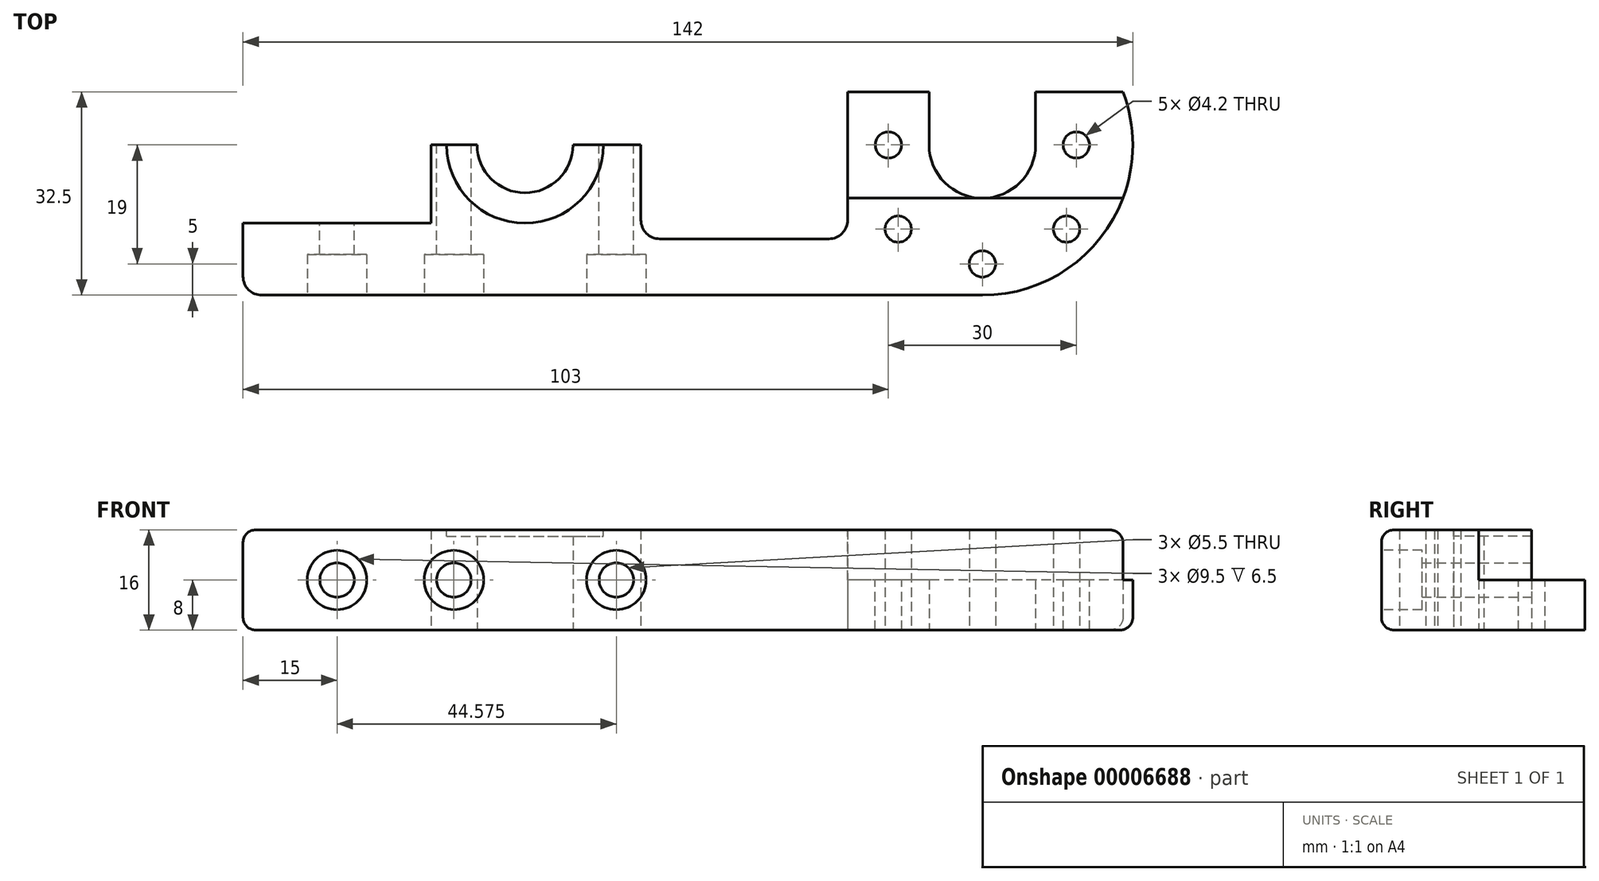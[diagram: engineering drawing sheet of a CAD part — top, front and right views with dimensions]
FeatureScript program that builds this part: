
annotation { "Feature Type Name" : "Feature", "Feature Type Description" : "" }
export const myFeature = defineFeature(function(context is Context, id is Id, definition is map)
    precondition{}
    {
        {
            var Q0;
            Q0=qCreatedBy(makeId("Top.planeOp"),FACE);
            var sketch = newSketch(context, id + "F0", { "sketchPlane" : qUnion([Q0])});
            skLineSegment(sketch, "E0", {"start": v(30, 20.5) * mm, "end": v(30, 8) * mm});
            skLineSegment(sketch, "E1", {"start": v(30, 8) * mm, "end": v(0, 8) * mm});
            skArc(sketch, "E2", {"start": v(37.35, 20.5) * mm, "mid": v(45, 12.85) * mm, "end": v(52.65, 20.5) * mm});
            skArc(sketch, "E3", {"start": v(109.5, 20.5) * mm, "mid": v(118, 12) * mm, "end": v(126.5, 20.5) * mm});
            skLineSegment(sketch, "E4.top", {"start": v(63.5, 5.5) * mm, "end": v(96.5, 5.5) * mm});
            skLineSegment(sketch, "E4.right", {"start": v(96.5, 29) * mm, "end": v(96.5, 5.5) * mm});
            skLineSegment(sketch, "E5.0", {"start": v(118, -3.5) * mm, "end": v(0, -3.5) * mm});
            skArc(sketch, "E6.trimOffspring", {"start": v(118, -3.5) * mm, "mid": v(137.75, 6.86) * mm, "end": v(140.44, 29) * mm});
            skLineSegment(sketch, "E7", {"start": v(0, 8) * mm, "end": v(0, -3.5) * mm});
            skPoint(sketch, "E8.center", {"position": v(0, 0) * mm});
            skCircle(sketch, "E9.3.0", {"center": v(104.56, 7.06) * mm, "radius": 2.1 * mm});
            skCircle(sketch, "E9.4.0", {"center": v(118, 1.5) * mm, "radius": 2.1 * mm});
            skCircle(sketch, "E9.5.0", {"center": v(131.44, 7.06) * mm, "radius": 2.1 * mm});
            skLineSegment(sketch, "E10", {"start": v(30, 20.5) * mm, "end": v(37.35, 20.5) * mm});
            skLineSegment(sketch, "E11", {"start": v(96.5, 29) * mm, "end": v(109.5, 29) * mm});
            skLineSegment(sketch, "E12.0", {"start": v(126.5, 20.5) * mm, "end": v(126.5, 29) * mm});
            skLineSegment(sketch, "E13.0", {"start": v(109.5, 20.5) * mm, "end": v(109.5, 29) * mm});
            skLineSegment(sketch, "E14.trimOffspring", {"start": v(126.5, 29) * mm, "end": v(140.44, 29) * mm});
            skLineSegment(sketch, "E15.trimOffspring", {"start": v(52.65, 20.5) * mm, "end": v(63.5, 20.5) * mm});
            skLineSegment(sketch, "E16.0", {"start": v(63.5, 20.5) * mm, "end": v(63.5, 5.5) * mm});
            skSolve(sketch);
        }
        {
            var Q0;
            Q0=makeQuery(id+"F0.imprint","IMPRINT",FACE,{"disambiguationData":[TD([[makeQuery(id+"F0.imprint","IMPRINT",EDGE,{"derivedFrom":sQuery(id+"F0.wireOp",EDGE,"E0")}),1.0]])]});
            extrude(context, id + "F1", {"entities" : qUnion([Q0]), "depth" : 16 * mm});
        }
        {
            var Q0;
            Q0=makeQuery(id+"F1.opExtrude","SWEPT_FACE",FACE,{"disambiguationData":[OSD([sQuery(id+"F0.wireOp",EDGE,"E4.right")])]});
            var sketch = newSketch(context, id + "F2", { "sketchPlane" : qUnion([Q0])});
            skLineSegment(sketch, "E17.top", {"start": v(-29, 16) * mm, "end": v(-12, 16) * mm});
            skLineSegment(sketch, "E17.left", {"start": v(-29, 8) * mm, "end": v(-29, 16) * mm});
            skLineSegment(sketch, "E18", {"start": v(-29, 8) * mm, "end": v(-12, 8) * mm});
            skPoint(sketch, "E17.bottom.end.orphan", {"position": v(-20.5, 0) * mm});
            skLineSegment(sketch, "E19.0", {"start": v(-12, 8) * mm, "end": v(-12, 16) * mm});
            skPoint(sketch, "E20.orphan", {"position": v(-20.5, 16) * mm});
            skSolve(sketch);
        }
        {
            var Q0;
            Q0 = qSketchRegion(id + "F2", true);
            extrude(context, id + "F3", {"entities" : qUnion([Q0]), "operationType" : NewBodyOperationType.REMOVE, "endBound" : BoundingType.THROUGH_ALL, "oppositeDirection" : true, "depth" : 25 * mm});
        }
        {
            var Q0;
            Q0=makeQuery(id+"F1.opExtrude","SWEPT_FACE",FACE,{"disambiguationData":[OSD([sQuery(id+"F0.wireOp",EDGE,"E15.trimOffspring")])]});
            var sketch = newSketch(context, id + "F4", { "sketchPlane" : qUnion([Q0])});
            skCircle(sketch, "E21", {"center": v(-59.58, 8) * mm, "radius": 2.75 * mm});
            skCircle(sketch, "E22", {"center": v(-33.65, 8) * mm, "radius": 2.75 * mm});
            skCircle(sketch, "E23", {"center": v(-15, 8) * mm, "radius": 2.75 * mm});
            skSolve(sketch);
        }
        {
            var Q0;
            Q0 = qSketchRegion(id + "F4", true);
            extrude(context, id + "F5", {"entities" : qUnion([Q0]), "operationType" : NewBodyOperationType.REMOVE, "endBound" : BoundingType.THROUGH_ALL, "oppositeDirection" : true, "depth" : 25 * mm});
        }
        {
            var Q0;
            Q0=makeQuery(id+"F1.opExtrude","SWEPT_EDGE",EDGE,{"disambiguationData":[OSD([sQuery(id+"F0.wireOp",EDGE,"E4.top"),sQuery(id+"F0.wireOp",EDGE,"E4.right")])]});
            var Q1;
            Q1=makeQuery(id+"F1.opExtrude","SWEPT_EDGE",EDGE,{"disambiguationData":[OSD([sQuery(id+"F0.wireOp",EDGE,"E4.top"),sQuery(id+"F0.wireOp",EDGE,"E4.left")])]});
            var Q2;
            Q2=makeQuery(id+"F1.opExtrude","SWEPT_EDGE",EDGE,{"disambiguationData":[OSD([sQuery(id+"F0.wireOp",EDGE,"E5.0"),sQuery(id+"F0.wireOp",EDGE,"E7")])]});
            fillet(context, id + "F6", {"entities" : qUnion([Q0, Q1, Q2]), "radius" : 3 * mm, "tangentPropagation" : true, "allowEdgeOverflow" : false});
        }
        {
            var Q0;
            {var subQ0=makeQuery(id+"F3.opExtrude","SWEPT_FACE",FACE,{"disambiguationData":[OSD([sQuery(id+"F2.wireOp",EDGE,"E18")])]});Q0=makeQuery(id+"F3.boolean.opBoolean","COPY",FACE,{"disambiguationData":[TD([makeQuery(id+"F1.opExtrude","SWEPT_FACE",FACE,{"disambiguationData":[OSD([sQuery(id+"F0.wireOp",EDGE,"E6.trimOffspring")])]})])],"derivedFrom":subQ0});}
            var sketch = newSketch(context, id + "F7", { "sketchPlane" : qUnion([Q0])});
            skLineSegment(sketch, "E24", {"start": v(126.5, 29) * mm, "end": v(126.5, 12) * mm, "construction": true});
            skLineSegment(sketch, "E25.0", {"start": v(103, 29) * mm, "end": v(103, 12) * mm, "construction": true});
            skLineSegment(sketch, "E26.0", {"start": v(133, 29) * mm, "end": v(133, 12) * mm, "construction": true});
            skLineSegment(sketch, "E27", {"start": v(133, 20.5) * mm, "end": v(103, 20.5) * mm, "construction": true});
            skCircle(sketch, "E28", {"center": v(133, 20.5) * mm, "radius": 2.1 * mm});
            skCircle(sketch, "E29", {"center": v(103, 20.5) * mm, "radius": 2.1 * mm});
            skSolve(sketch);
        }
        {
            var Q0;
            Q0 = qSketchRegion(id + "F7", true);
            extrude(context, id + "F8", {"entities" : qUnion([Q0]), "operationType" : NewBodyOperationType.REMOVE, "endBound" : BoundingType.THROUGH_ALL, "oppositeDirection" : true, "depth" : 25 * mm});
        }
        {
            var Q0;
            Q0=makeQuery(id+"F1.opExtrude","CAP_FACE",FACE,{"disambiguationData":[OSD([sQuery(id+"F0.wireOp",EDGE,"E0"),sQuery(id+"F0.wireOp",EDGE,"E1"),sQuery(id+"F0.wireOp",EDGE,"E2"),sQuery(id+"F0.wireOp",EDGE,"E3"),sQuery(id+"F0.wireOp",EDGE,"E4.top"),sQuery(id+"F0.wireOp",EDGE,"E4.left"),sQuery(id+"F0.wireOp",EDGE,"E4.right"),sQuery(id+"F0.wireOp",EDGE,"E5.0"),sQuery(id+"F0.wireOp",EDGE,"E6.trimOffspring"),sQuery(id+"F0.wireOp",EDGE,"E7"),sQuery(id+"F0.wireOp",EDGE,"E9.3.0"),sQuery(id+"F0.wireOp",EDGE,"E9.4.0"),sQuery(id+"F0.wireOp",EDGE,"E9.5.0"),sQuery(id+"F0.wireOp",EDGE,"E10"),sQuery(id+"F0.wireOp",EDGE,"E11"),sQuery(id+"F0.wireOp",EDGE,"E12.0"),sQuery(id+"F0.wireOp",EDGE,"E13.0"),sQuery(id+"F0.wireOp",EDGE,"E14.trimOffspring"),sQuery(id+"F0.wireOp",EDGE,"E15.trimOffspring")])],"isStart":false});
            var sketch = newSketch(context, id + "F9", { "sketchPlane" : qUnion([Q0])});
            skCircle(sketch, "E30", {"center": v(45, 20.5) * mm, "radius": 12.5 * mm});
            skSolve(sketch);
        }
        {
            var Q0;
            Q0 = qSketchRegion(id + "F9", true);
            extrude(context, id + "F10", {"entities" : qUnion([Q0]), "operationType" : NewBodyOperationType.REMOVE, "oppositeDirection" : true, "depth" : 1 * mm});
        }
        {
            var Q0;
            Q0=makeQuery(id+"F1.opExtrude","CAP_EDGE",EDGE,{"disambiguationData":[OSD([sQuery(id+"F0.wireOp",EDGE,"E7")])],"isStart":false});
            var Q1;
            Q1=makeQuery(id+"F1.opExtrude","CAP_EDGE",EDGE,{"disambiguationData":[OSD([sQuery(id+"F0.wireOp",EDGE,"E7")])],"isStart":true});
            fillet(context, id + "F11", {"entities" : qUnion([Q0, Q1]), "radius" : 2 * mm, "tangentPropagation" : true, "allowEdgeOverflow" : false});
        }
        {
            var Q0;
            Q0=makeQuery(id+"F1.opExtrude","SWEPT_FACE",FACE,{"disambiguationData":[OSD([sQuery(id+"F0.wireOp",EDGE,"E5.0")])]});
            var sketch = newSketch(context, id + "F12", { "sketchPlane" : qUnion([Q0])});
            skCircle(sketch, "E31", {"center": v(15, 8) * mm, "radius": 4.75 * mm});
            skCircle(sketch, "E32", {"center": v(33.65, 8) * mm, "radius": 4.75 * mm});
            skCircle(sketch, "E33", {"center": v(59.57, 8) * mm, "radius": 4.75 * mm});
            skSolve(sketch);
        }
        {
            var Q0;
            Q0 = qSketchRegion(id + "F12", true);
            extrude(context, id + "F13", {"entities" : qUnion([Q0]), "operationType" : NewBodyOperationType.REMOVE, "oppositeDirection" : true, "depth" : 6.5 * mm});
        }
    });
